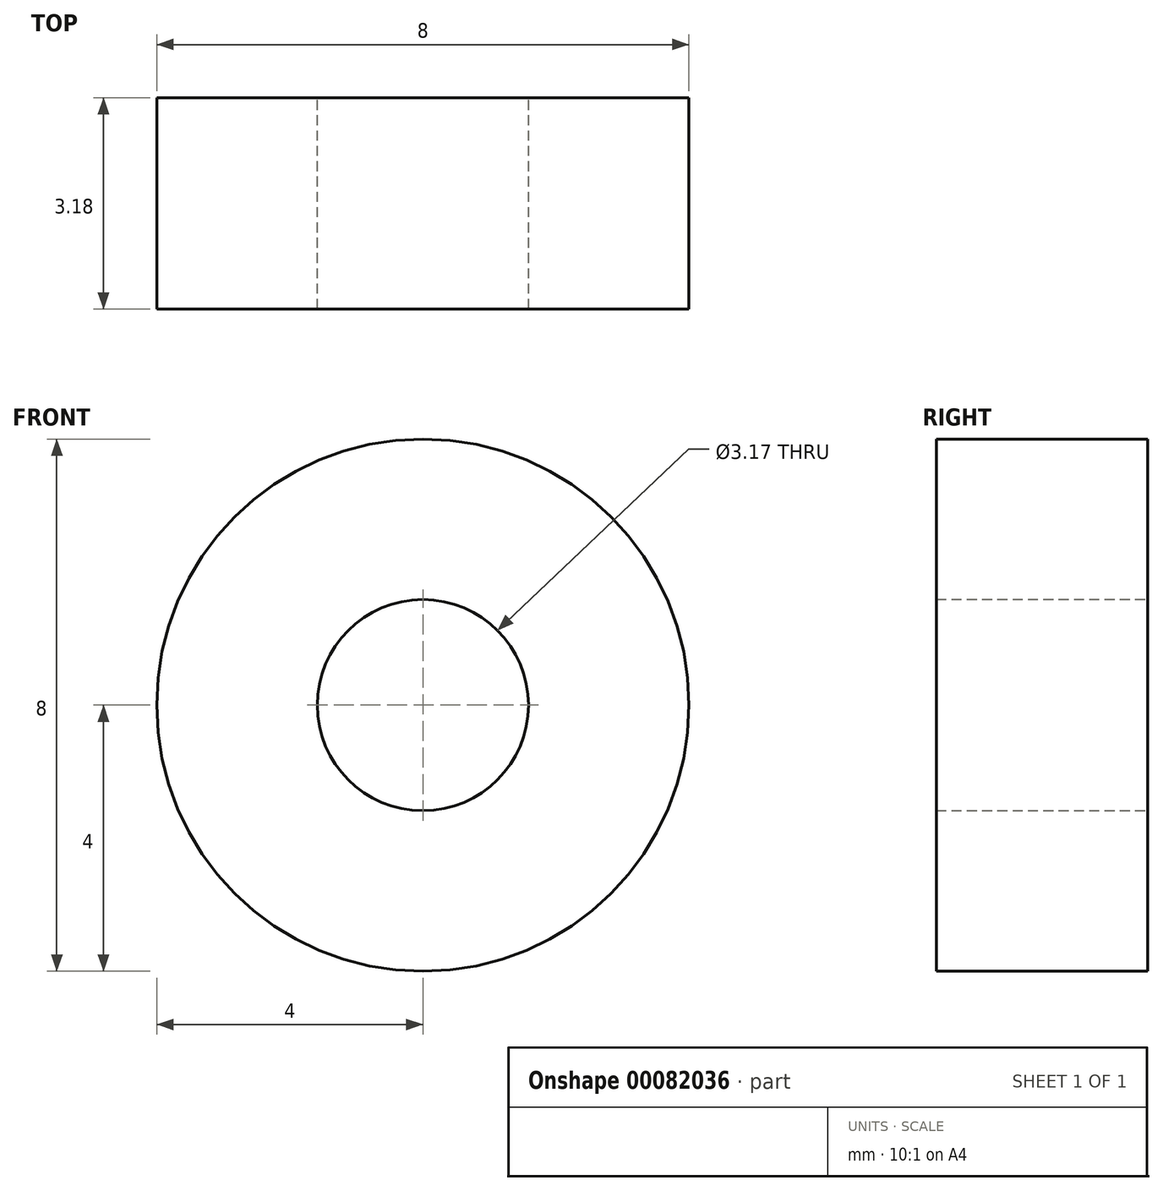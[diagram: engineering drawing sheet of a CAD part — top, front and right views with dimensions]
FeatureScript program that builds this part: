
annotation { "Feature Type Name" : "Feature", "Feature Type Description" : "" }
export const myFeature = defineFeature(function(context is Context, id is Id, definition is map)
    precondition{}
    {
        {
            var Q0;
            Q0=qCreatedBy(makeId("Front.planeOp"),FACE);
            var sketch = newSketch(context, id + "F0", { "sketchPlane" : qUnion([Q0])});
            skCircle(sketch, "E0", {"center": v(0, 0) * mm, "radius": 4 * mm});
            skCircle(sketch, "E1", {"center": v(0, 0) * mm, "radius": 1.59 * mm});
            skSolve(sketch);
        }
        {
            var Q0;
            Q0 = qSketchRegion(id + "F0", true);
            extrude(context, id + "F1", {"entities" : qUnion([Q0]), "depth" : 3.17 * mm});
        }
    });
